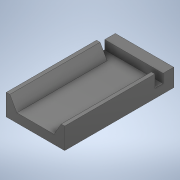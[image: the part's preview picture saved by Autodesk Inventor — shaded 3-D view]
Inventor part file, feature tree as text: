
AUTODESK INVENTOR PART (.ipt)
format: ipt  version: 2020 (Build 240168000, 168)  size: 127,488 bytes
history: native  units: mm
features: extrude x3, sketch x3, projected_geometry x2, other x1
ambient origin geometry x8: Origin, YZ Plane, XZ Plane, XY Plane, X Axis, Y Axis, Z Axis, Center Point
bodies: Body1 (feature_tree)
feature tree (9):
  other  "Твердое тело1"
  extrude  "Выдавливание1"  Depth=30.8mm
  extrude  "Выдавливание2"  Depth=16.5mm
  extrude  "Выдавливание3"  Depth=2.5mm TaperAngle=0.0deg
  sketch  "Эскиз1"
  sketch  "Эскиз2"
  projected_geometry  "Спроецированная петля1"
  sketch  "Эскиз3"
  projected_geometry  "Спроецированная петля2"
